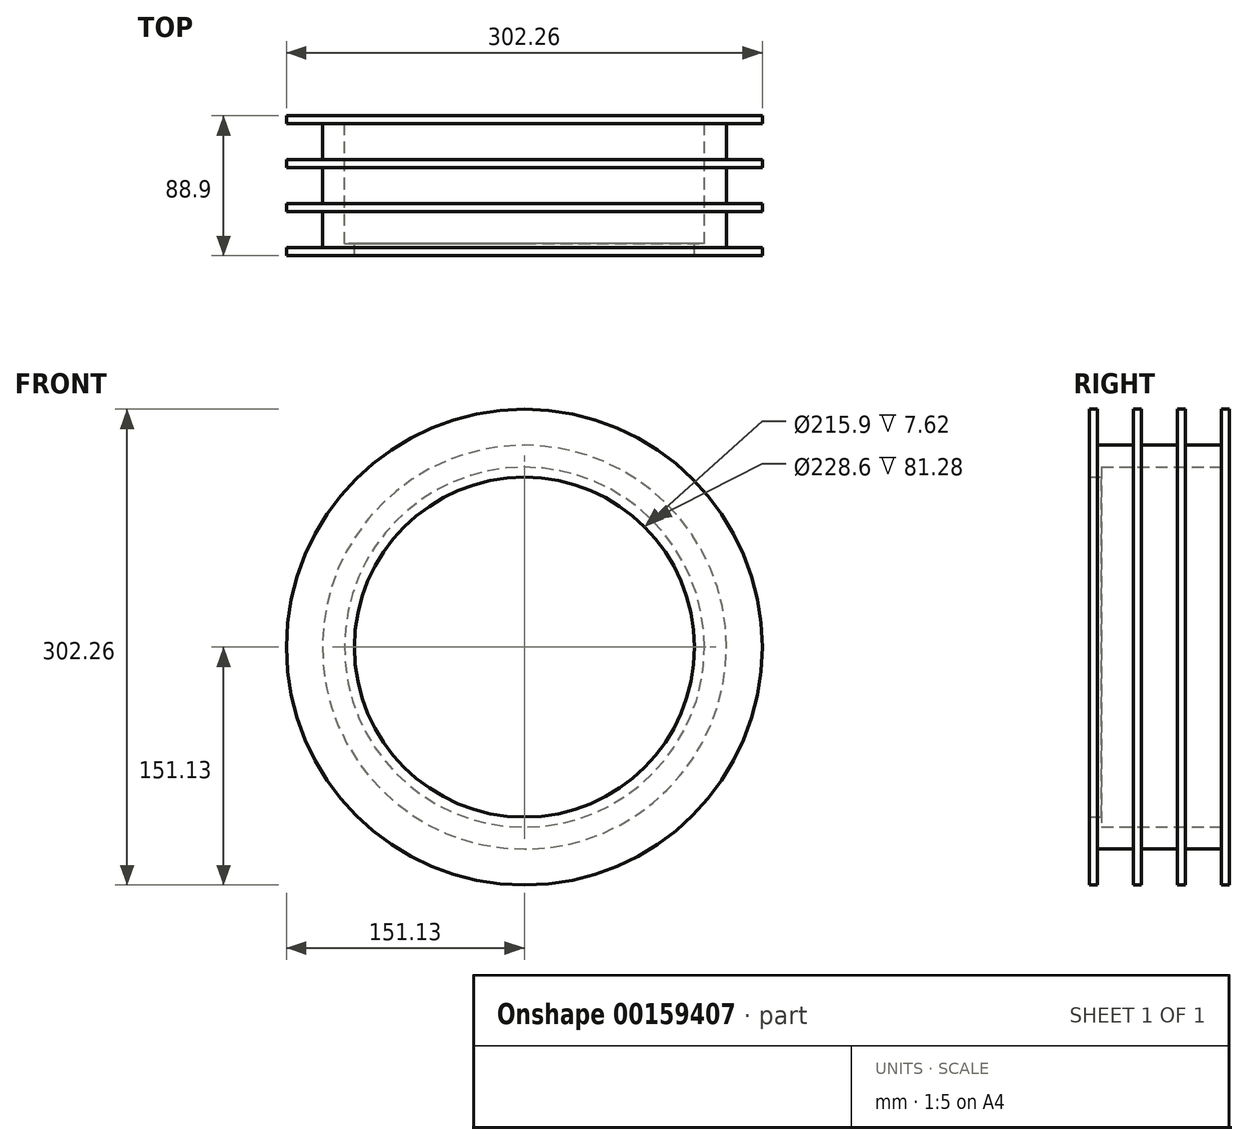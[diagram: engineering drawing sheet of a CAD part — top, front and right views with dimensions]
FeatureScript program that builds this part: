
annotation { "Feature Type Name" : "Feature", "Feature Type Description" : "" }
export const myFeature = defineFeature(function(context is Context, id is Id, definition is map)
    precondition{}
    {
        {
            var Q0;
            Q0=qCreatedBy(makeId("Front.planeOp"),FACE);
            var sketch = newSketch(context, id + "F0", { "sketchPlane" : qUnion([Q0])});
            skCircle(sketch, "E0", {"center": v(0, 0) * mm, "radius": 151.13 * mm});
            skSolve(sketch);
        }
        {
            var Q0;
            Q0=makeQuery(id+"F0.imprint","IMPRINT",FACE,{"disambiguationData":[TD([[makeQuery(id+"F0.imprint","IMPRINT",EDGE,{"derivedFrom":sQuery(id+"F0.wireOp",EDGE,"E0")}),1.0]])]});
            extrude(context, id + "F1", {"entities" : qUnion([Q0]), "depth" : 5.08 * mm});
        }
        {
            var Q0;
            Q0=makeQuery(id+"F1.opExtrude","CAP_FACE",FACE,{"disambiguationData":[OSD([sQuery(id+"F0.wireOp",EDGE,"E0")])],"isStart":true});
            var sketch = newSketch(context, id + "F2", { "sketchPlane" : qUnion([Q0])});
            skCircle(sketch, "E1", {"center": v(0, 0) * mm, "radius": 128.27 * mm});
            skSolve(sketch);
        }
        {
            var Q0;
            Q0=makeQuery(id+"F2.imprint","IMPRINT",FACE,{"disambiguationData":[TD([[makeQuery(id+"F2.imprint","IMPRINT",EDGE,{"derivedFrom":sQuery(id+"F2.wireOp",EDGE,"E1")}),1.0]])]});
            extrude(context, id + "F3", {"entities" : qUnion([Q0]), "operationType" : NewBodyOperationType.ADD, "depth" : 11.43 * mm});
        }
        {
            var Q0;
            Q0=makeQuery(id+"F3.opExtrude","CAP_FACE",FACE,{"disambiguationData":[OSD([sQuery(id+"F2.wireOp",EDGE,"E1")])],"isStart":false});
            var sketch = newSketch(context, id + "F4", { "sketchPlane" : qUnion([Q0])});
            skCircle(sketch, "E2", {"center": v(0, 0) * mm, "radius": 107.95 * mm});
            skSolve(sketch);
        }
        {
            var Q0;
            Q0=sQuery(id+"F4.wireOp",VERTEX,"E2.center");
            var Q1;
            Q1=makeQuery(id+"F1.opExtrude","SWEPT_BODY",BODY,{"disambiguationData":[OSD([sQuery(id+"F0.wireOp",EDGE,"E0")])]});
            hole(context, id + "F5", {"style" : HoleStyle.SIMPLE, "endStyle" : HoleEndStyle.THROUGH, "holeDiameter" : 215.9 * mm, "locations" : qUnion([Q0]), "scope" : qUnion([Q1]), "isTappedThrough" : true});
        }
        {
            var Q0;
            Q0=makeQuery(id+"F1.opExtrude","SWEPT_BODY",BODY,{"disambiguationData":[OSD([sQuery(id+"F0.wireOp",EDGE,"E0")])]});
            var Q1;
            Q1=makeQuery(id+"F3.opExtrude","CAP_FACE",FACE,{"disambiguationData":[OSD([sQuery(id+"F2.wireOp",EDGE,"E1")])],"isStart":false});
            mirror(context, id + "F6", {"operationType" : NewBodyOperationType.ADD, "entities" : qUnion([Q0]), "mirrorPlane" : qUnion([Q1])});
        }
        {
            var Q0;
            Q0=makeQuery(id+"F6.opPattern","COPY",FACE,{"derivedFrom":makeQuery(id+"F1.opExtrude","CAP_FACE",FACE,{"disambiguationData":[OSD([sQuery(id+"F0.wireOp",EDGE,"E0")])],"isStart":false}),"instanceName":"1"});
            var sketch = newSketch(context, id + "F7", { "sketchPlane" : qUnion([Q0])});
            skCircle(sketch, "E3", {"center": v(0, 0) * mm, "radius": 128.27 * mm});
            skSolve(sketch);
        }
        {
            var Q0;
            Q0=makeQuery(id+"F7.imprint","IMPRINT",FACE,{"disambiguationData":[TD([[makeQuery(id+"F7.imprint","IMPRINT",EDGE,{"derivedFrom":sQuery(id+"F7.wireOp",EDGE,"E3")}),1.0]])]});
            extrude(context, id + "F8", {"entities" : qUnion([Q0]), "operationType" : NewBodyOperationType.ADD, "depth" : 11.43 * mm});
        }
        {
            var Q0;
            Q0=makeQuery(id+"F1.opExtrude","SWEPT_BODY",BODY,{"disambiguationData":[OSD([sQuery(id+"F0.wireOp",EDGE,"E0")])]});
            var Q1;
            Q1=makeQuery(id+"F8.opExtrude","CAP_FACE",FACE,{"disambiguationData":[OSD([sQuery(id+"F0.wireOp",EDGE,"E0"),sQuery(id+"F5.hole-0.sketch.wireOp",EDGE,"core_line_2"),sQuery(id+"F7.wireOp",EDGE,"E3")])],"isStart":false});
            mirror(context, id + "F9", {"operationType" : NewBodyOperationType.ADD, "entities" : qUnion([Q0]), "mirrorPlane" : qUnion([Q1])});
        }
        {
            var Q0;
            Q0=makeQuery(id+"F9.opPattern","COPY",FACE,{"derivedFrom":makeQuery(id+"F1.opExtrude","CAP_FACE",FACE,{"disambiguationData":[OSD([sQuery(id+"F0.wireOp",EDGE,"E0")])],"isStart":false}),"instanceName":"1"});
            var sketch = newSketch(context, id + "F10", { "sketchPlane" : qUnion([Q0])});
            skCircle(sketch, "E4", {"center": v(0, 0) * mm, "radius": 114.3 * mm});
            skSolve(sketch);
        }
        {
            var Q0;
            Q0=makeQuery(id+"F10.imprint","IMPRINT",FACE,{"disambiguationData":[TD([[makeQuery(id+"F10.imprint","IMPRINT",EDGE,{"derivedFrom":sQuery(id+"F10.wireOp",EDGE,"E4")}),1.0]])]});
            extrude(context, id + "F11", {"entities" : qUnion([Q0]), "operationType" : NewBodyOperationType.REMOVE, "oppositeDirection" : true, "depth" : 81.28 * mm});
        }
    });
